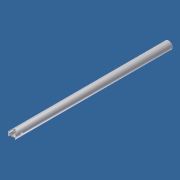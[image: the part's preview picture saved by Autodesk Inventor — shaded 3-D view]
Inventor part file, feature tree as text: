
AUTODESK INVENTOR PART (.ipt)
format: ipt  version: 2012 (Build 160160000, 160)  size: 97,280 bytes
history: native  units: in
note: dims shown in document units (in); Inventor stores cm internally (conversion verified against a paired STEP export)
features: extrude x3, sketch x3, plane x1, other x1
ambient origin geometry x8: Origin, YZ Plane, XZ Plane, XY Plane, X Axis, Y Axis, Z Axis, Center Point
bodies: Solid1 (feature_tree)
feature tree (8):
  extrude  "Extrusion1"  Depth=1.375in
  plane  "Work Plane2"
  extrude  "Extrusion2"  TaperAngle=0.0deg  [1 undecoded]
  extrude  "Extrusion3"  Depth=1.75in TaperAngle=0.0deg
  sketch  "Sketch1"  dims[d0=1.625in d1=1.375in]
  other  "Work Axis1"
  sketch  "Sketch2"  dims[d2=32.5in d3=0.0in d4=0.0in]
  sketch  "Sketch3"  dims[d5=1.325in d6=1.75in d7=0.0in d8=1.25in d9=0.5in d10=1.75in d11=0.0in]
note: 1 required parameter value undecoded (feature->parameter linkage not recoverable at this tier; creation-order binding heuristic only, values carry confidence <= 0.55)
